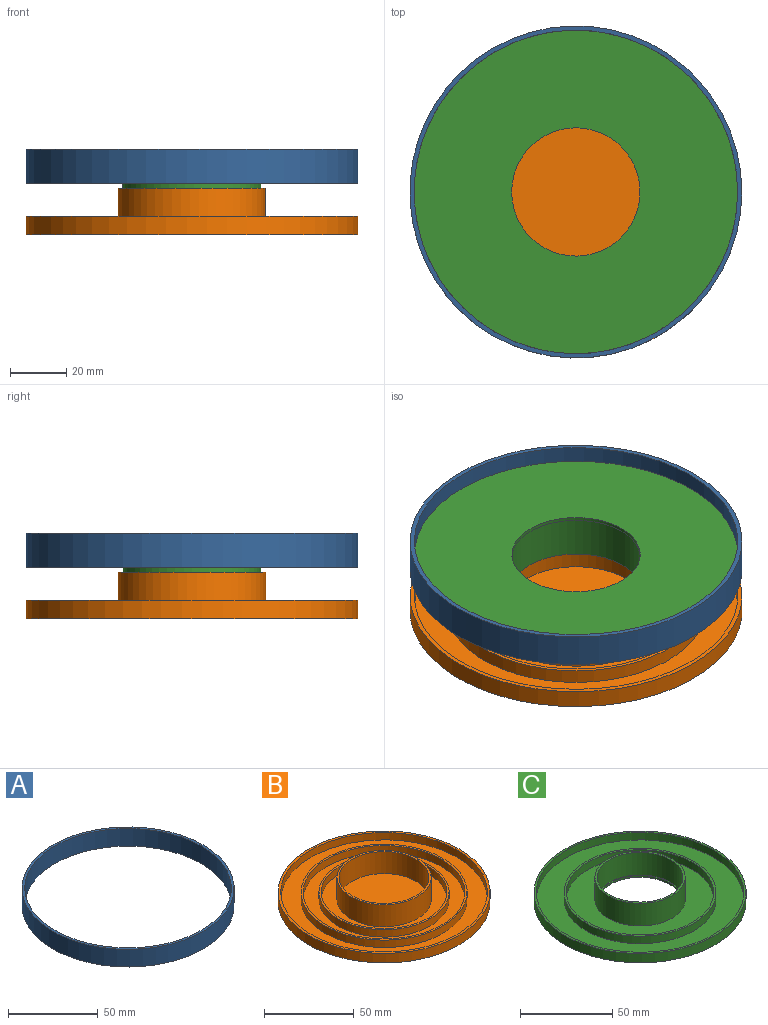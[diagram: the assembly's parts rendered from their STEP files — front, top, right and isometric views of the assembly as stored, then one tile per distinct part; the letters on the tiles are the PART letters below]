
ASSEMBLY  parts=3 mates=2
PART A: 4 faces, bbox 118x118x12 mm
  f0: cylinder r=57.5mm len=115mm, axis (0,0,1), area 4335.4mm2, adj f2,f3
  f1: cylinder r=59mm len=118mm, axis (0,0,1), area 4448.5mm2, adj f2,f3
  f2: plane 118x118mm, normal (0,0,1), area 549mm2, adj f0,f1
  f3: plane 118x118mm, normal (0,0,-1), area 549mm2, adj f0,f1
PART B: 17 faces, bbox 118x118x16.5 mm
  f0: cylinder r=46.2mm len=92.4mm, axis (0,0,1), area 1451.4mm2, adj f2,f7
  f1: cylinder r=45mm len=90mm, axis (0,0,1), area 1413.7mm2, adj f2,f8
  f2: plane 92.4x92.4mm, normal (0,0,1), area 343.8mm2, adj f0,f1
  f3: plane 118x118mm, normal (0,0,-1), area 10935.9mm2, adj f4
  f4: cylinder r=59mm len=118mm, axis (0,0,1), area 2409.6mm2, adj f3,f5
  f5: plane 118x118mm, normal (0,0,1), area 549mm2, adj f4,f6
  f6: cylinder r=57.5mm len=115mm, axis (0,0,1), area 1806.4mm2, adj f5,f7
  f7: plane 115x115mm, normal (0,0,1), area 3681.3mm2, adj f0,f6
  f8: plane 90x90mm, normal (0,0,1), area 2244.9mm2, adj f1,f14
  f9: cylinder r=25mm len=50mm, axis (0,0,1), area 2356.2mm2, adj f11,f16
  f10: cylinder r=26.2mm len=52.4mm, axis (0,0,1), area 2469.3mm2, adj f11,f12
  f11: plane 52.4x52.4mm, normal (0,0,1), area 193mm2, adj f9,f10
  f12: plane 70x70mm, normal (0,0,1), area 1691.9mm2, adj f10,f15
  f13: plane 72.4x72.4mm, normal (0,0,1), area 268.4mm2, adj f14,f15
  f14: cylinder r=36.2mm len=72.4mm, axis (0,0,1), area 1137.3mm2, adj f8,f13
  f15: cylinder r=35mm len=70mm, axis (0,0,1), area 1099.6mm2, adj f12,f13
  f16: plane 50x50mm, normal (0,0,1), area 1963.5mm2, adj f9
PART C: 14 faces, bbox 115x115x16.2 mm
  f0: cylinder r=40mm len=80mm, axis (0,0,1), area 1256.6mm2, adj f2,f3
  f1: cylinder r=41.2mm len=82.4mm, axis (0,0,1), area 1294.3mm2, adj f2,f11
  f2: plane 82.4x82.4mm, normal (0,0,1), area 306.1mm2, adj f0,f1
  f3: plane 80x80mm, normal (0,0,1), area 3140.8mm2, adj f0,f5
  f4: cylinder r=23.3mm len=46.6mm, axis (0,0,1), area 2196mm2, adj f6,f7
  f5: cylinder r=24.5mm len=49mm, axis (0,0,1), area 2309.1mm2, adj f3,f6
  f6: plane 49x49mm, normal (0,0,1), area 180.2mm2, adj f4,f5
  f7: plane 46.6x46.6mm, normal (0,0,1), area 72.4mm2, adj f4,f12
  f8: cylinder r=57.5mm len=115mm, axis (0,0,1), area 2240mm2, adj f10,f13
  f9: cylinder r=56.3mm len=112.6mm, axis (0,0,1), area 1768.7mm2, adj f10,f11
  f10: plane 115x115mm, normal (0,0,1), area 429mm2, adj f8,f9
  f11: plane 112.6x112.6mm, normal (0,0,1), area 4625.2mm2, adj f1,f9
  f12: cylinder r=22.8mm len=45.6mm, axis (0,0,1), area 171.9mm2, adj f7,f13
  f13: plane 115x115mm, normal (0,0,-1), area 8753.8mm2, adj f8,f12
PLACE A t=(-86.06,-13.39,30.35)mm
PLACE B t=(-86.06,-13.39,13.52)mm
PLACE C rot(axis=(0,-1,0),180deg) t=(-86.06,-13.39,35.25)mm
MATE fastened A.f0 <-> C.f0  axis (0,0,1) through (-86.06,-13.39,36.35)mm
MATE slider B.f0 <-> C.f0  axis (0,0,1) through (-86.06,-13.39,21.02)mm
